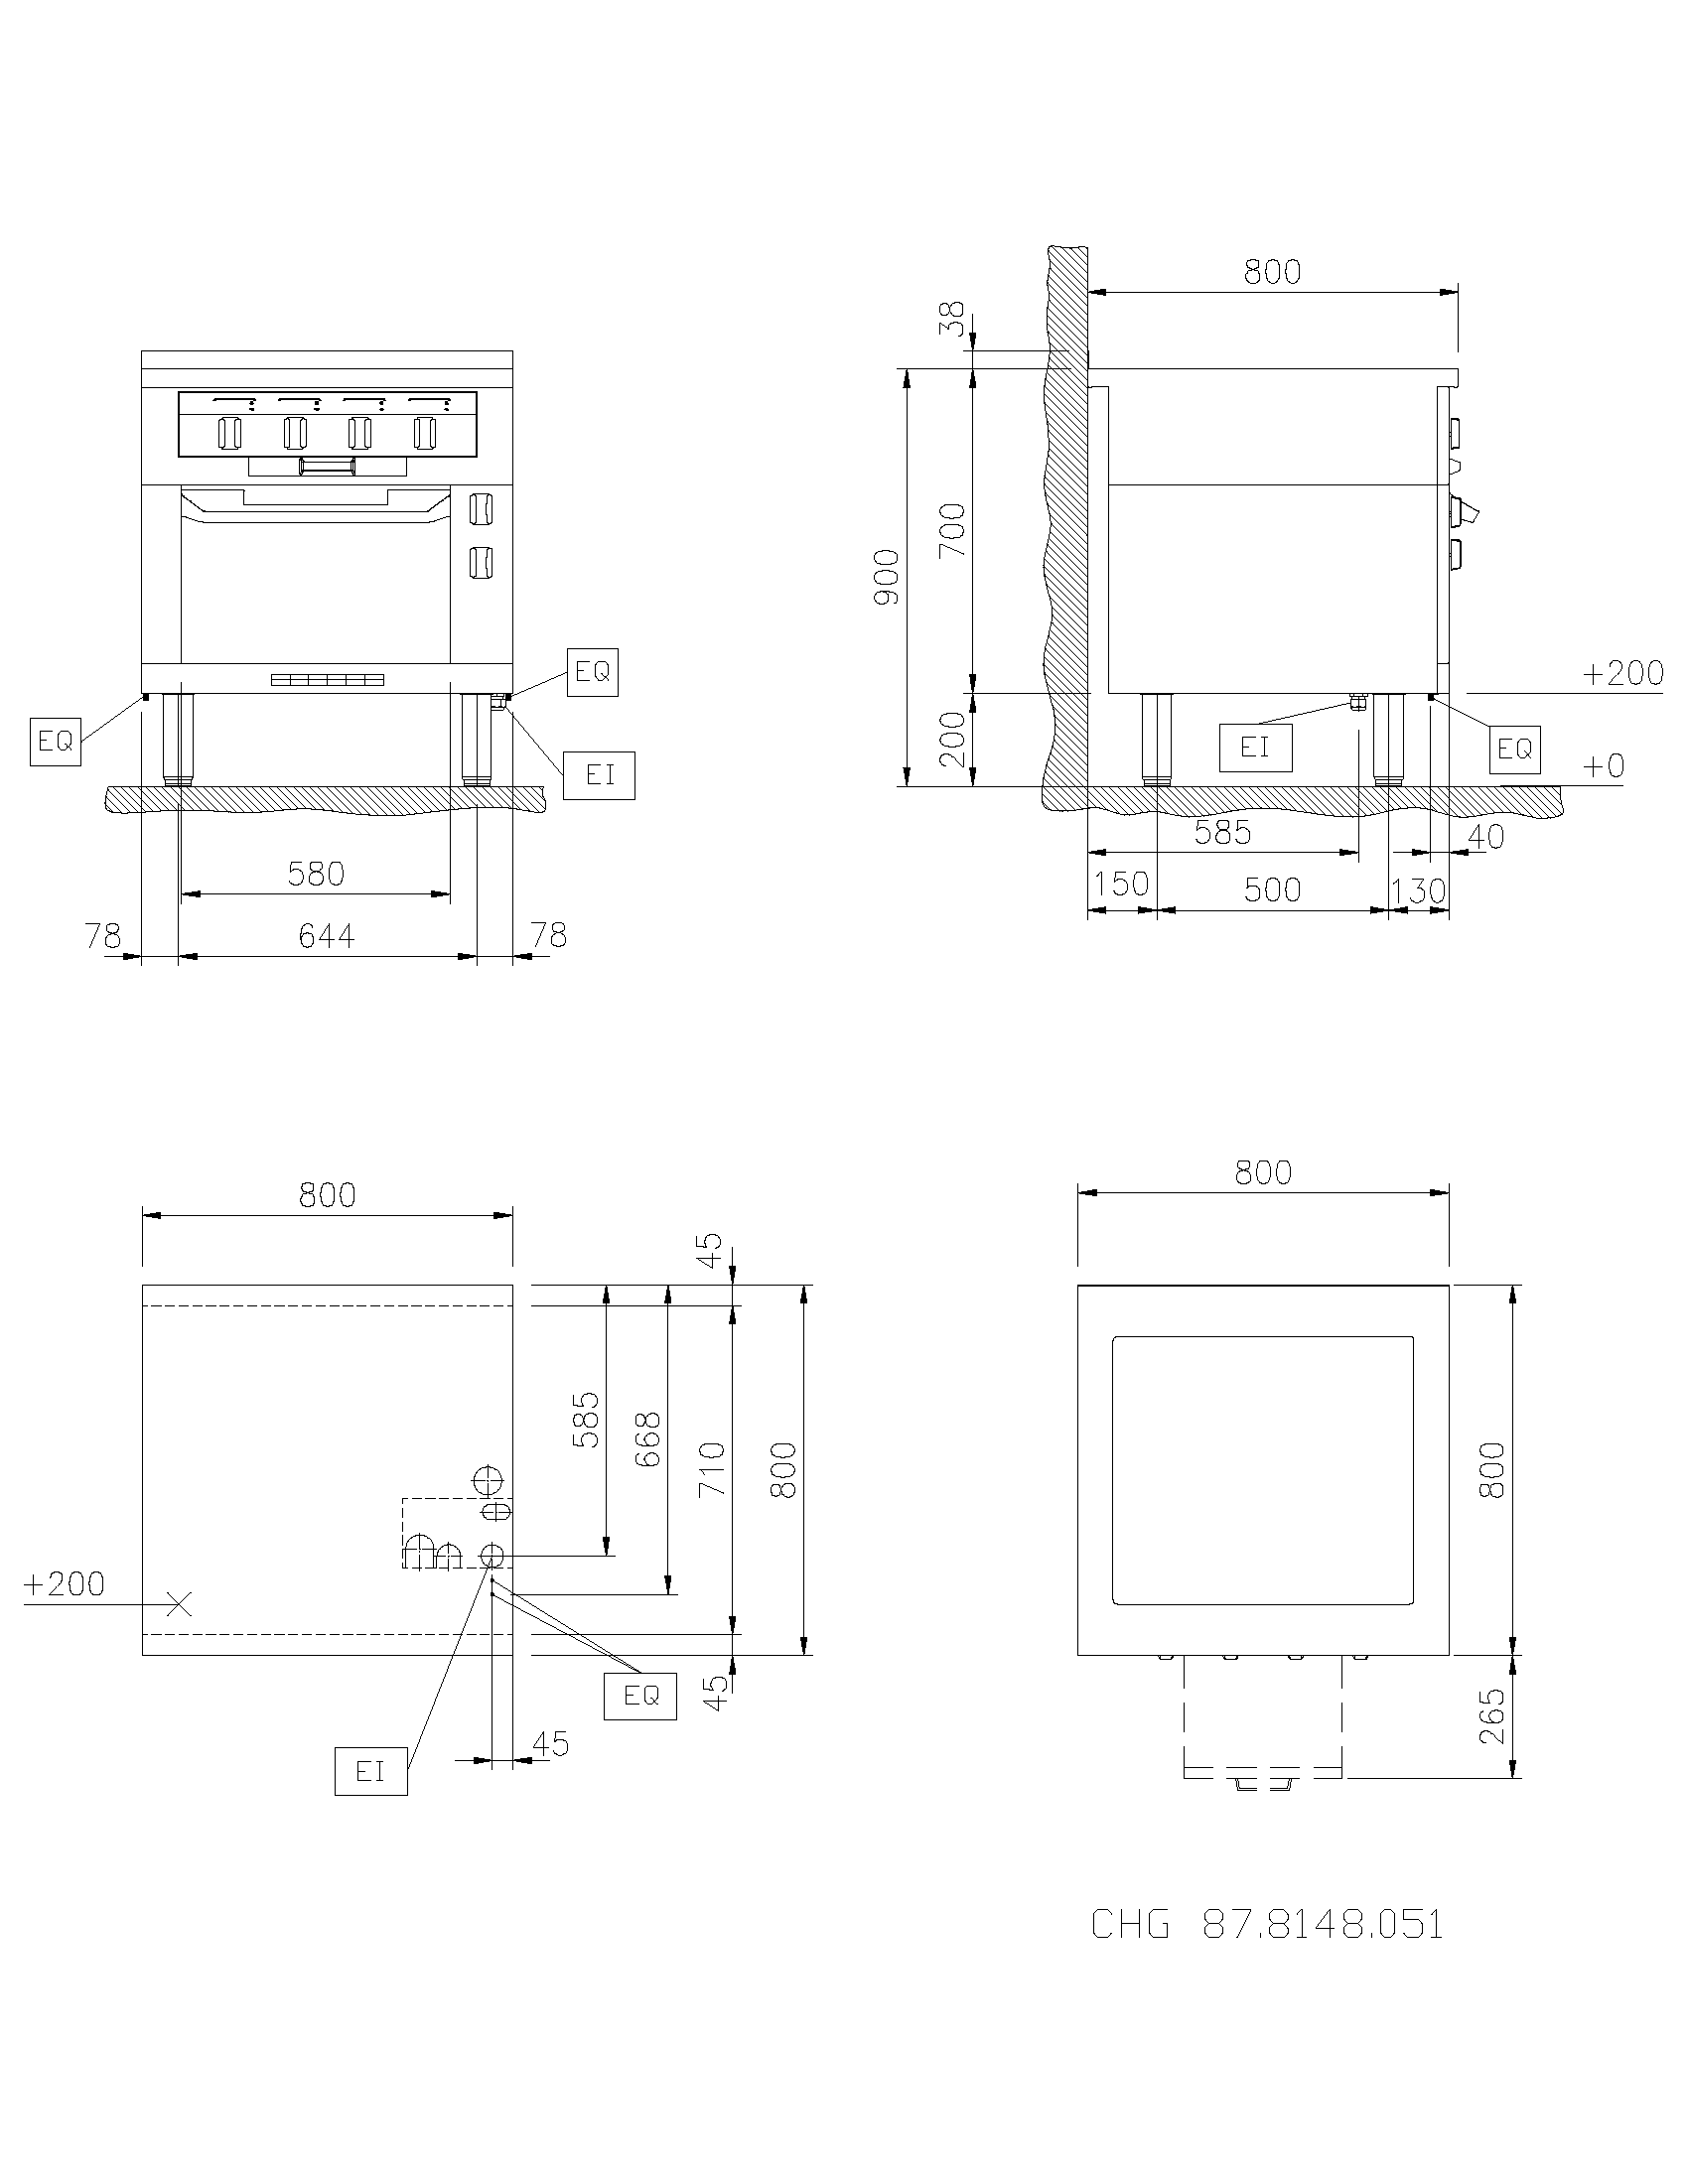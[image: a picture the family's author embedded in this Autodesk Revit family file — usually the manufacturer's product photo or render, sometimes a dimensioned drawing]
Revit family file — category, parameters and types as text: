
# Revit family: QF_ELECTROLUXPROFESSIONAL_588419_MALNFCH8AO
name_source: partatom
category: Attrezzature speciali
units: mm (PartAtom-declared; Revit-internal decimal feet)

## family parameters
Basato su piano di lavoro = No
Condiviso = No
Punto di calcolo locali = No
Quota connettore circolare = Usa diametro
Sempre verticale = Sì
Taglio con vuoti quando caricato = No
Tipo di parte = Normale

## types (1)
- Standard
    Accessory = Sì
    Cold Water Size = 0"
    Compressed Air Pressure = 0.00 psi
    Compressed Air Size = 0"
    Compressed Air Volume = 0 GPM
    Condensate Return Size = 0"
    Cycle = 50 Hz
    Depth Actual = 800 mm  [stored 2.62467 ft]
    Descrizione = EL.SOLID TOP,ST.OV,PASS,2S,800X800X800H
    Direct Waste Size = 0"
    Gas Input Pressure = 0.0
    Gas KW = 0
    Gas Size = 0"
    HP = 23.2 HP
    Height Actual = 800 mm  [stored 2.62467 ft]
    Hot Water Size = 0"
    Item Number = 588419
    Length Actual = 800 mm  [stored 2.62467 ft]
    Modello = MALNFCH8AO
    Phase = 3
    Produttore = Electrolux Professional
    Prospetto di default = 0 mm  [stored 0 ft]
    Refrigerant Compressor Remote = Sì
    Refrigeration Liquid Line Size = 0 mm  [stored 0 ft]
    Refrigeration Suction Line Size = 0 mm  [stored 0 ft]
    Steam Consumption per Hour = 0
    Steam Supply Maximum Pressure = 0.00 psi
    Steam Supply Minimum Pressure = 0.00 psi
    Steam Supply Size = 0"
    URL = https://www.electroluxprofessional.com
    URL Manufacturer = https://www.electroluxprofessional.com
    Volts = 400 V
    Watts = 17300 W
    Weight = 211.00 kg

note: source unit labels omitted for Gas Input Pressure — the stored unit's dimension contradicts the parameter name (converter mislabeling)

note: [stored X ft] marks values corroborated as IEEE doubles in the binary element streams (Revit-internal decimal feet)

## geometry (parser evidence)
native form markers: Sweep x14
no freeform markers — native parametric forms only
